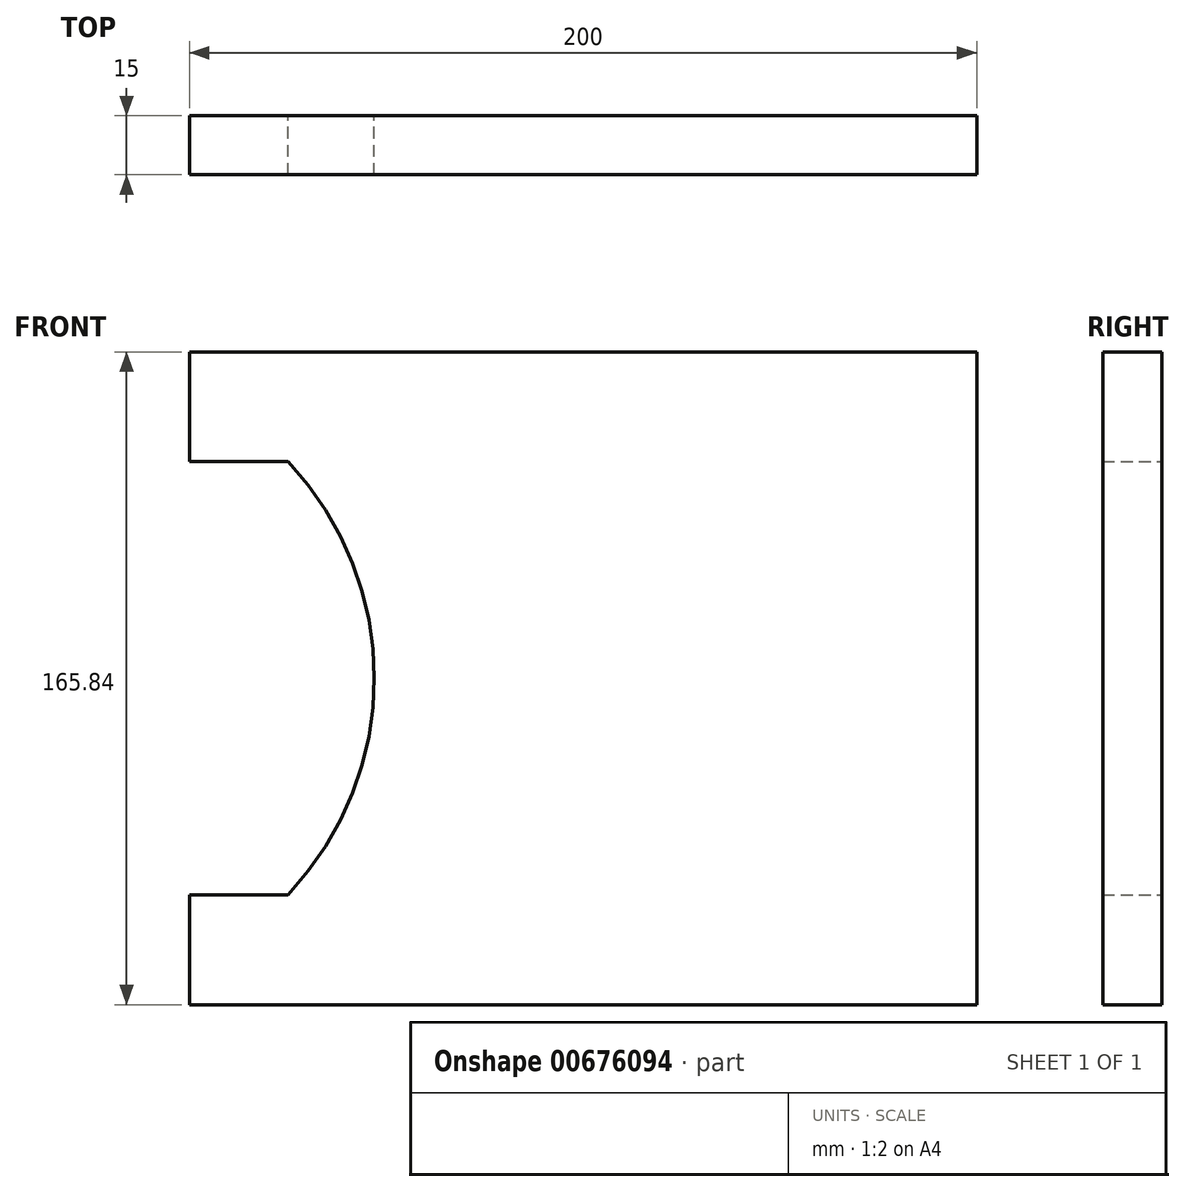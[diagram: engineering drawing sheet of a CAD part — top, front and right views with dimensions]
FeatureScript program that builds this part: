
annotation { "Feature Type Name" : "Feature", "Feature Type Description" : "" }
export const myFeature = defineFeature(function(context is Context, id is Id, definition is map)
    precondition{}
    {
        {
            var Q0;
            Q0=qCreatedBy(makeId("Front.planeOp"),FACE);
            var sketch = newSketch(context, id + "F0", { "sketchPlane" : qUnion([Q0])});
            skLineSegment(sketch, "E0.bottom", {"start": v(100, 82.92) * mm, "end": v(-100, 82.92) * mm});
            skLineSegment(sketch, "E0.top", {"start": v(100, -82.92) * mm, "end": v(-100, -82.92) * mm});
            skLineSegment(sketch, "E0.left", {"start": v(100, 82.92) * mm, "end": v(100, -82.92) * mm});
            skLineSegment(sketch, "E0.right", {"start": v(-100, 82.92) * mm, "end": v(-100, 55.03) * mm});
            skPoint(sketch, "E0.middle", {"position": v(0, 0) * mm});
            skLineSegment(sketch, "E1", {"start": v(-100, 55.03) * mm, "end": v(-75, 55.03) * mm});
            skLineSegment(sketch, "E2", {"start": v(-75, -54.97) * mm, "end": v(-100, -54.97) * mm});
            skArc(sketch, "E3", {"start": v(-75, -54.97) * mm, "mid": v(-53.1, 0.03) * mm, "end": v(-75, 55.02) * mm});
            skLineSegment(sketch, "E4.trimOffspring", {"start": v(-100, -54.97) * mm, "end": v(-100, -82.92) * mm});
            skSolve(sketch);
        }
        {
            var Q0;
            Q0 = qSketchRegion(id + "F0", true);
            extrude(context, id + "F1", {"entities" : qUnion([Q0]), "depth" : 15 * mm, "offsetDistance" : 25 * mm});
        }
    });
